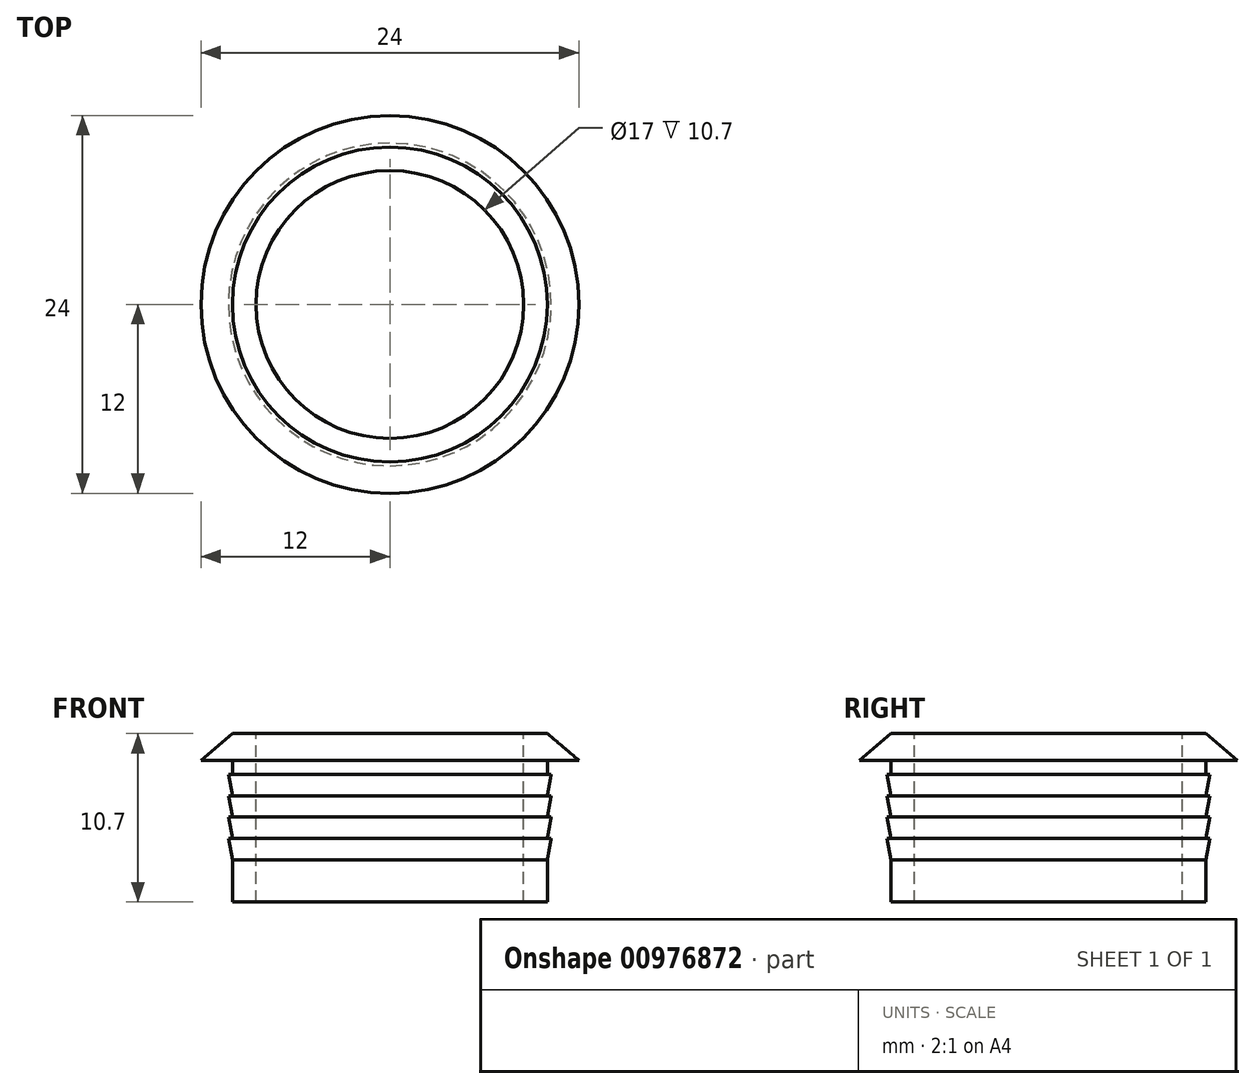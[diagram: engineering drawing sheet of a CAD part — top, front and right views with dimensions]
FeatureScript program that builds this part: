
annotation { "Feature Type Name" : "Feature", "Feature Type Description" : "" }
export const myFeature = defineFeature(function(context is Context, id is Id, definition is map)
    precondition{}
    {
        {
            var Q0;
            Q0=qCreatedBy(makeId("Front.planeOp"),FACE);
            var sketch = newSketch(context, id + "F0", { "sketchPlane" : qUnion([Q0])});
            skLineSegment(sketch, "E0.bottom", {"start": v(-10, -4.5) * mm, "end": v(0, -4.5) * mm});
            skLineSegment(sketch, "E0.left", {"start": v(-10, -4.5) * mm, "end": v(-10, -1.82) * mm});
            skPoint(sketch, "E0.middle", {"position": v(0, 0) * mm});
            skLineSegment(sketch, "E1", {"start": v(-12, 4.5) * mm, "end": v(-10, 6.2) * mm});
            skLineSegment(sketch, "E2", {"start": v(-10, 6.2) * mm, "end": v(0, 6.2) * mm});
            skLineSegment(sketch, "E3", {"start": v(-12, 4.5) * mm, "end": v(-10, 4.5) * mm});
            skLineSegment(sketch, "E4", {"start": v(0, 6.2) * mm, "end": v(0, -4.5) * mm});
            skLineSegment(sketch, "E5", {"start": v(-10.25, 4.5) * mm, "end": v(-10.25, -4.5) * mm, "construction": true});
            skLineSegment(sketch, "E6", {"start": v(-10, 3.6) * mm, "end": v(0, 3.6) * mm, "construction": true});
            skLineSegment(sketch, "E7", {"start": v(-10, 3.6) * mm, "end": v(-10.25, 3.6) * mm});
            skLineSegment(sketch, "E8", {"start": v(-10, 2.25) * mm, "end": v(-10.25, 2.25) * mm});
            skLineSegment(sketch, "E9.trimOffspring", {"start": v(-10, 3.6) * mm, "end": v(-10, 4.5) * mm});
            skLineSegment(sketch, "E10", {"start": v(-10, 0.9) * mm, "end": v(-10.25, 0.9) * mm});
            skLineSegment(sketch, "E11", {"start": v(-10, -0.46) * mm, "end": v(-10.25, -0.46) * mm});
            skLineSegment(sketch, "E12", {"start": v(-10.25, -0.46) * mm, "end": v(-10, -1.82) * mm});
            skLineSegment(sketch, "E13", {"start": v(-10.25, 3.6) * mm, "end": v(-10, 2.25) * mm});
            skLineSegment(sketch, "E14", {"start": v(-10.25, 2.25) * mm, "end": v(-10, 0.9) * mm});
            skLineSegment(sketch, "E15", {"start": v(-10.25, 0.9) * mm, "end": v(-10, -0.46) * mm});
            skSolve(sketch);
        }
        {
            var Q0;
            Q0=makeQuery(id+"F0.imprint","IMPRINT",FACE,{"disambiguationData":[TD([[makeQuery(id+"F0.imprint","IMPRINT",EDGE,{"derivedFrom":sQuery(id+"F0.wireOp",EDGE,"E0.bottom")}),1.0]])]});
            var Q1;
            Q1=sQuery(id+"F0.wireOp",EDGE,"E4");
            revolve(context, id + "F1", {"surfaceOperationType" : NewSurfaceOperationType.NEW, "entities" : qUnion([Q0]), "axis" : qUnion([Q1]), "revolveType" : RevolveType.FULL});
        }
        {
            var Q0;
            Q0=makeQuery(id+"F1.opRevolve","SWEPT_FACE",FACE,{"disambiguationData":[OSD([sQuery(id+"F0.wireOp",EDGE,"E2")])]});
            var sketch = newSketch(context, id + "F2", { "sketchPlane" : qUnion([Q0])});
            skCircle(sketch, "E16", {"center": v(0, 0) * mm, "radius": 8.5 * mm});
            skSolve(sketch);
        }
        {
            var Q0;
            Q0=sQuery(id+"F2.wireOp",VERTEX,"E16.center");
            var Q1;
            Q1=makeQuery(id+"F1.opRevolve","SWEPT_BODY",BODY,{"disambiguationData":[OSD([sQuery(id+"F0.wireOp",EDGE,"E0.bottom"),sQuery(id+"F0.wireOp",EDGE,"E0.left"),sQuery(id+"F0.wireOp",EDGE,"E1"),sQuery(id+"F0.wireOp",EDGE,"E2"),sQuery(id+"F0.wireOp",EDGE,"E3"),sQuery(id+"F0.wireOp",EDGE,"E4"),sQuery(id+"F0.wireOp",EDGE,"E7"),sQuery(id+"F0.wireOp",EDGE,"NWlTcinP-1cxs-jLVc-qtn8-pO3xiqXShVAJ"),sQuery(id+"F0.wireOp",EDGE,"E8"),sQuery(id+"F0.wireOp",EDGE,"ESjylO2L-JHWp-R1WB-Pyn0-KqrXKHrRkmGF"),sQuery(id+"F0.wireOp",EDGE,"E9.trimOffspring"),sQuery(id+"F0.wireOp",EDGE,"b0f39884-6230-4be2-8e48-8a134c90df3a.trimOffspring"),sQuery(id+"F0.wireOp",EDGE,"E10"),sQuery(id+"F0.wireOp",EDGE,"efhlfdGQ-sKxb-jqz9-GuBv-DnlZjZ8UCQB4"),sQuery(id+"F0.wireOp",EDGE,"f9fbf725-2e6d-47a3-a27d-d5d1557c6c6d.trimOffspring"),sQuery(id+"F0.wireOp",EDGE,"E11"),sQuery(id+"F0.wireOp",EDGE,"E12"),sQuery(id+"F0.wireOp",EDGE,"b00abd19-cadf-4ae0-83ab-543a50aa5407.trimOffspring")])]});
            hole(context, id + "F3", {"style" : HoleStyle.SIMPLE, "endStyle" : HoleEndStyle.THROUGH, "holeDiameter" : 17 * mm, "majorDiameter" : 5 * mm, "isTappedThrough" : true, "tappedDepth" : 12 * mm, "tapClearance" : 3, "locations" : qUnion([Q0]), "scope" : qUnion([Q1])});
        }
    });
